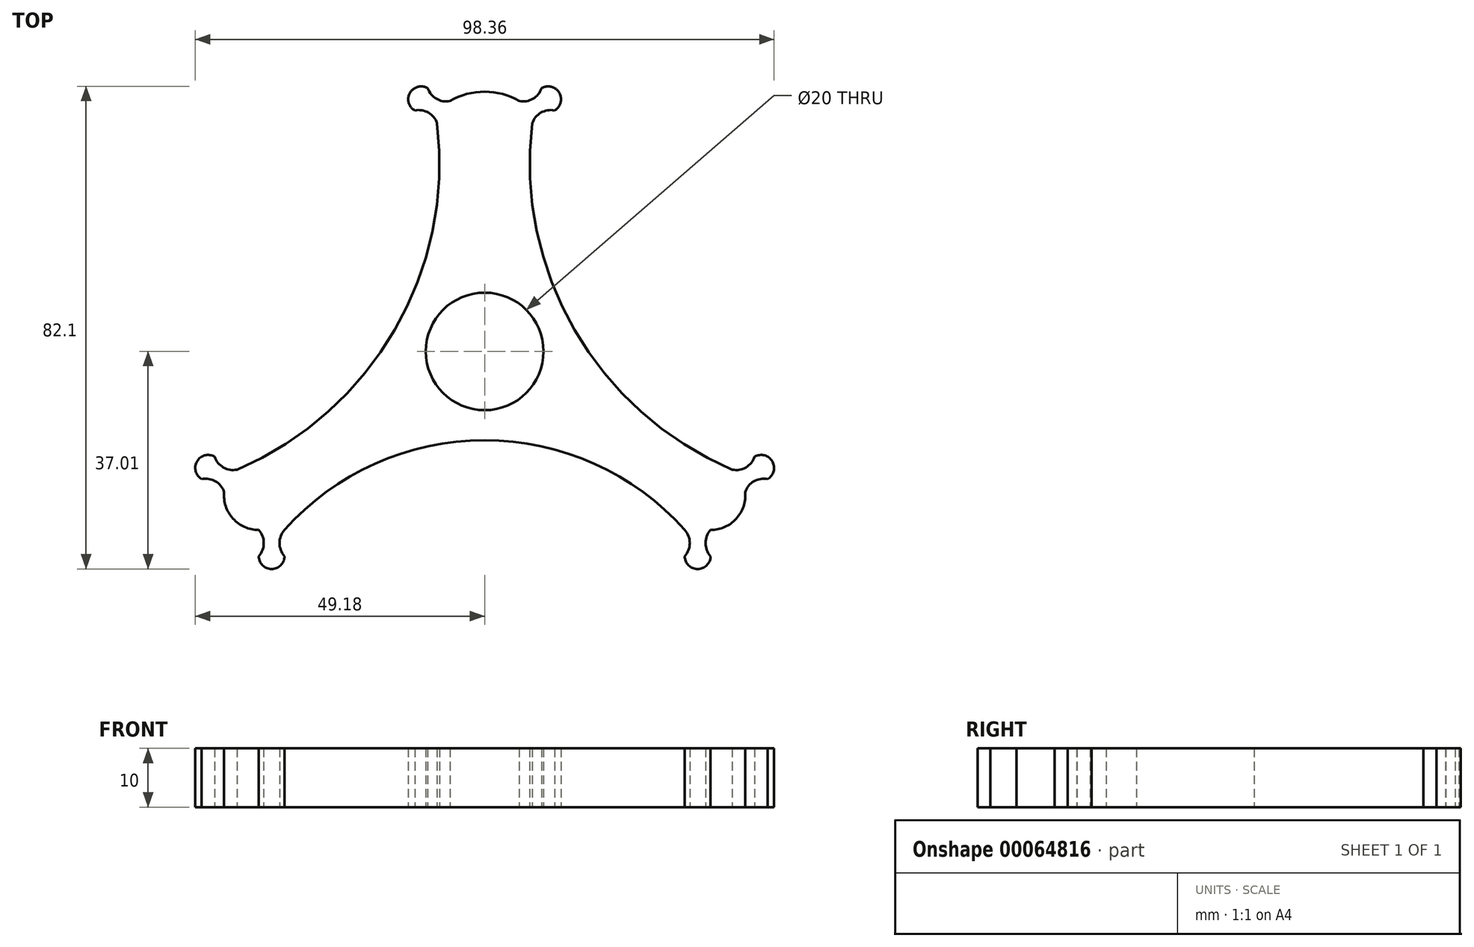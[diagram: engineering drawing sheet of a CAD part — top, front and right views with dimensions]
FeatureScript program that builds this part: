
annotation { "Feature Type Name" : "Feature", "Feature Type Description" : "" }
export const myFeature = defineFeature(function(context is Context, id is Id, definition is map)
    precondition{}
    {
        {
            var Q0;
            Q0=qCreatedBy(makeId("Top.planeOp"),FACE);
            var sketch = newSketch(context, id + "F0", { "sketchPlane" : qUnion([Q0])});
            skCircle(sketch, "E0", {"center": v(0, 0) * mm, "radius": 10 * mm});
            skCircle(sketch, "E1", {"center": v(0, 0) * mm, "radius": 15 * mm});
            skPoint(sketch, "E2", {"position": v(-25.07, 9.34) * mm});
            skLineSegment(sketch, "E3", {"start": v(-25.07, 9.34) * mm, "end": v(-8.07, 38.78) * mm, "construction": true});
            skLineSegment(sketch, "E4", {"start": v(-25.07, 9.34) * mm, "end": v(-42.07, -20.1) * mm, "construction": true});
            skLineSegment(sketch, "E5.MirrorCS", {"start": v(25.07, 9.34) * mm, "end": v(8.07, 38.78) * mm, "construction": true});
            skLineSegment(sketch, "E6.MirrorCS", {"start": v(25.07, 9.34) * mm, "end": v(42.07, -20.1) * mm, "construction": true});
            skLineSegment(sketch, "E7", {"start": v(0, -30.38) * mm, "end": v(-34, -30.38) * mm, "construction": true});
            skPoint(sketch, "E8", {"position": v(0, -30.38) * mm});
            skLineSegment(sketch, "E9", {"start": v(0, -30.38) * mm, "end": v(34, -30.38) * mm, "construction": true});
            skPoint(sketch, "E10", {"position": v(-5.87, 42.6) * mm});
            skPoint(sketch, "E11", {"position": v(-44.27, -23.92) * mm});
            skPoint(sketch, "E12.MirrorP", {"position": v(5.87, 42.6) * mm});
            skPoint(sketch, "E13.MirrorP", {"position": v(44.27, -23.92) * mm});
            skPoint(sketch, "E14", {"position": v(-38.4, -30.38) * mm});
            skPoint(sketch, "E15", {"position": v(38.4, -30.38) * mm});
            skLineSegment(sketch, "E16", {"start": v(-25.07, 9.34) * mm, "end": v(-30.13, 12.26) * mm});
            skLineSegment(sketch, "E17", {"start": v(25.07, 9.34) * mm, "end": v(27.99, 11.02) * mm});
            skLineSegment(sketch, "E18", {"start": v(0, -30.38) * mm, "end": v(0, -34.69) * mm});
            skArc(sketch, "E19", {"start": v(8.07, 38.78) * mm, "mid": v(15.27, 3.68) * mm, "end": v(42.07, -20.1) * mm});
            skArc(sketch, "E20.MirrorCS", {"start": v(-8.07, 38.78) * mm, "mid": v(-15.27, 3.68) * mm, "end": v(-42.07, -20.1) * mm});
            skArc(sketch, "E21", {"start": v(34, -30.38) * mm, "mid": v(0, -15.12) * mm, "end": v(-34, -30.38) * mm});
            skArc(sketch, "E22", {"start": v(-38.4, -34.83) * mm, "mid": v(-37.54, -32.6) * mm, "end": v(-38.4, -30.38) * mm});
            skArc(sketch, "E23.MirrorCS", {"start": v(-34, -34.83) * mm, "mid": v(-34.86, -32.6) * mm, "end": v(-34, -30.38) * mm});
            skArc(sketch, "E24", {"start": v(-38.4, -34.83) * mm, "mid": v(-36.2, -37.01) * mm, "end": v(-34, -34.83) * mm});
            skArc(sketch, "E25.MirrorCS", {"start": v(34, -34.83) * mm, "mid": v(34.86, -32.6) * mm, "end": v(34, -30.38) * mm});
            skArc(sketch, "E26.MirrorCS", {"start": v(38.4, -34.83) * mm, "mid": v(37.54, -32.6) * mm, "end": v(38.4, -30.38) * mm});
            skArc(sketch, "E27.MirrorCS", {"start": v(38.4, -34.83) * mm, "mid": v(36.2, -37.01) * mm, "end": v(34, -34.83) * mm});
            skArc(sketch, "E28", {"start": v(-44.27, -23.92) * mm, "mid": v(-45.76, -22.1) * mm, "end": v(-48.08, -21.72) * mm});
            skArc(sketch, "E29", {"start": v(-45.88, -17.9) * mm, "mid": v(-44.4, -19.73) * mm, "end": v(-42.07, -20.1) * mm});
            skArc(sketch, "E30", {"start": v(-45.88, -17.9) * mm, "mid": v(-48.89, -18.71) * mm, "end": v(-48.08, -21.72) * mm});
            skArc(sketch, "E31", {"start": v(-44.27, -23.92) * mm, "mid": v(-42.77, -28.45) * mm, "end": v(-38.4, -30.38) * mm});
            skArc(sketch, "E32.MirrorCS", {"start": v(-11.88, 40.98) * mm, "mid": v(-9.56, 40.6) * mm, "end": v(-8.07, 38.78) * mm});
            skArc(sketch, "E33.MirrorCS", {"start": v(-5.87, 42.6) * mm, "mid": v(-8.2, 42.97) * mm, "end": v(-9.68, 44.8) * mm});
            skArc(sketch, "E34.MirrorCS", {"start": v(-11.88, 40.98) * mm, "mid": v(-12.69, 43.99) * mm, "end": v(-9.68, 44.8) * mm});
            skArc(sketch, "E35.MirrorCS", {"start": v(5.87, 42.6) * mm, "mid": v(8.2, 42.97) * mm, "end": v(9.68, 44.8) * mm});
            skArc(sketch, "E36.MirrorCS", {"start": v(11.88, 40.98) * mm, "mid": v(9.56, 40.6) * mm, "end": v(8.07, 38.78) * mm});
            skArc(sketch, "E37.MirrorCS", {"start": v(11.88, 40.98) * mm, "mid": v(12.69, 43.99) * mm, "end": v(9.68, 44.8) * mm});
            skArc(sketch, "E38.MirrorCS", {"start": v(45.88, -17.9) * mm, "mid": v(44.4, -19.73) * mm, "end": v(42.07, -20.1) * mm});
            skArc(sketch, "E39.MirrorCS", {"start": v(44.27, -23.92) * mm, "mid": v(45.76, -22.1) * mm, "end": v(48.08, -21.72) * mm});
            skArc(sketch, "E40.MirrorCS", {"start": v(45.88, -17.9) * mm, "mid": v(48.89, -18.71) * mm, "end": v(48.08, -21.72) * mm});
            skArc(sketch, "E41.MirrorCS", {"start": v(44.27, -23.92) * mm, "mid": v(42.77, -28.45) * mm, "end": v(38.4, -30.38) * mm});
            skArc(sketch, "E42", {"start": v(5.87, 42.6) * mm, "mid": v(0, 44.18) * mm, "end": v(-5.87, 42.6) * mm});
            skSolve(sketch);
        }
        {
            var Q0;
            Q0=makeQuery(id+"F0.imprint","IMPRINT",FACE,{"disambiguationData":[TD([[makeQuery(id+"F0.imprint","IMPRINT",EDGE,{"derivedFrom":sQuery(id+"F0.wireOp",EDGE,"E0")}),-1.0]])]});
            var Q1;
            Q1=makeQuery(id+"F0.imprint","IMPRINT",FACE,{"disambiguationData":[TD([[makeQuery(id+"F0.imprint","IMPRINT",EDGE,{"derivedFrom":sQuery(id+"F0.wireOp",EDGE,"E1")}),-1.0]])]});
            var Q2;
            Q2=makeQuery(id+"F0.imprint","IMPRINT",FACE,{"disambiguationData":[TD([[makeQuery(id+"F0.imprint","IMPRINT",EDGE,{"derivedFrom":sQuery(id+"F0.wireOp",EDGE,"rauPZceA-AvJe-wY7d-aHQx-y0BkBm7dZX6A")}),1.0]])]});
            var Q3;
            {var subQ0=sQuery(id+"F0.wireOp",EDGE,"66c77fe6-8d23-4775-9337-49077d0eecb40.MirrorCS");Q3=makeQuery(id+"F0.imprint","IMPRINT",FACE,{"disambiguationData":[TD([[makeQuery(id+"F0.imprint","IMPRINT",EDGE,{"derivedFrom":subQ0}),-1.0]])]});}
            var Q4;
            {var subQ0=sQuery(id+"F0.wireOp",EDGE,"f178b5fa-dc7a-4bd1-90cf-9f9022b9a26d0.MirrorCS");Q4=makeQuery(id+"F0.imprint","IMPRINT",FACE,{"disambiguationData":[TD([[makeQuery(id+"F0.imprint","IMPRINT",EDGE,{"derivedFrom":subQ0}),1.0]])]});}
            var Q5;
            {var subQ0=sQuery(id+"F0.wireOp",EDGE,"766df824-92d9-44e2-9a4e-65756bf51aea");var subQ1=makeQuery(id+"F0.imprint","INTERSECT",VERTEX,{"derivedFrom":[subQ0,sQuery(id+"F0.wireOp",EDGE,"f178b5fa-dc7a-4bd1-90cf-9f9022b9a26d0.MirrorCS")]});Q5=makeQuery(id+"F0.imprint","IMPRINT",FACE,{"disambiguationData":[TD([[makeQuery(id+"F0.imprint","IMPRINT",EDGE,{"disambiguationData":[TD([[subQ1,-1.0]])],"derivedFrom":subQ0}),1.0]])]});}
            var Q6;
            {var subQ0=sQuery(id+"F0.wireOp",EDGE,"218adaf4-7306-4dce-b0c2-e02d0b1e01730.MirrorCS");Q6=makeQuery(id+"F0.imprint","IMPRINT",FACE,{"disambiguationData":[TD([[makeQuery(id+"F0.imprint","IMPRINT",EDGE,{"derivedFrom":subQ0}),-1.0]])]});}
            var Q7;
            {var subQ0=sQuery(id+"F0.wireOp",EDGE,"57e329e2-70f2-4a0c-8648-4a172ac2a8620.MirrorCS");Q7=makeQuery(id+"F0.imprint","IMPRINT",FACE,{"disambiguationData":[TD([[makeQuery(id+"F0.imprint","IMPRINT",EDGE,{"derivedFrom":subQ0}),1.0]])]});}
            var Q8;
            {var subQ0=sQuery(id+"F0.wireOp",EDGE,"7f4108d4-b1d3-4f68-b26e-f25bcda3abed");var subQ1=makeQuery(id+"F0.imprint","INTERSECT",VERTEX,{"derivedFrom":[subQ0,sQuery(id+"F0.wireOp",EDGE,"57e329e2-70f2-4a0c-8648-4a172ac2a8620.MirrorCS")]});Q8=makeQuery(id+"F0.imprint","IMPRINT",FACE,{"disambiguationData":[TD([[makeQuery(id+"F0.imprint","IMPRINT",EDGE,{"disambiguationData":[TD([[subQ1,-1.0]])],"derivedFrom":subQ0}),1.0]])]});}
            var Q9;
            {var subQ0=sQuery(id+"F0.wireOp",EDGE,"7BR6bjah-HHM2-aaMn-V7ne-WDie43C7rssP");Q9=makeQuery(id+"F0.imprint","IMPRINT",FACE,{"disambiguationData":[TD([[makeQuery(id+"F0.imprint","IMPRINT",EDGE,{"derivedFrom":subQ0}),-1.0]])]});}
            var Q10;
            {var subQ0=sQuery(id+"F0.wireOp",EDGE,"68eed4c9-a6f2-48c1-af04-7bd5d963a1a60.MirrorCS");Q10=makeQuery(id+"F0.imprint","IMPRINT",FACE,{"disambiguationData":[TD([[makeQuery(id+"F0.imprint","IMPRINT",EDGE,{"derivedFrom":subQ0}),1.0]])]});}
            var Q11;
            {var subQ4=sQuery(id+"F0.wireOp",EDGE,"ZnVcgLQC-YPiM-oc29-vfqV-L4HdhOj6Hgbx");Q11=makeQuery(id+"F0.imprint","IMPRINT",FACE,{"disambiguationData":[TD([[makeQuery(id+"F0.imprint","IMPRINT",EDGE,{"derivedFrom":subQ4}),1.0]])]});}
            var Q12;
            {var subQ0=sQuery(id+"F0.wireOp",EDGE,"ZnVcgLQC-YPiM-oc29-vfqV-L4HdhOj6Hgbx");Q12=makeQuery(id+"F0.imprint","IMPRINT",FACE,{"disambiguationData":[TD([[makeQuery(id+"F0.imprint","IMPRINT",EDGE,{"derivedFrom":subQ0}),-1.0]])]});}
            var Q13;
            {var subQ0=sQuery(id+"F0.wireOp",EDGE,"e4d09ac3-73be-4e2f-9fd0-e6afb1f81fb40.MirrorC");var subQ1=makeQuery(id+"F0.imprint","INTERSECT",VERTEX,{"derivedFrom":[subQ0,sQuery(id+"F0.wireOp",EDGE,"GvBOSrXI-6s7b-nos9-OxcZ-QlSHfa4bqhK4")]});Q13=makeQuery(id+"F0.imprint","IMPRINT",FACE,{"disambiguationData":[TD([[makeQuery(id+"F0.imprint","IMPRINT",EDGE,{"disambiguationData":[TD([[subQ1,-1.0]])],"derivedFrom":subQ0}),-1.0]])]});}
            var Q14;
            Q14=makeQuery(id+"F0.imprint","IMPRINT",FACE,{"disambiguationData":[TD([[makeQuery(id+"F0.imprint","IMPRINT",EDGE,{"derivedFrom":sQuery(id+"F0.wireOp",EDGE,"hSSR9ah8-QHQd-FjbW-g9Ed-Mq7VvAuAAHpD")}),-1.0]])]});
            var Q15;
            Q15=makeQuery(id+"F0.imprint","IMPRINT",FACE,{"disambiguationData":[TD([[makeQuery(id+"F0.imprint","IMPRINT",EDGE,{"derivedFrom":sQuery(id+"F0.wireOp",EDGE,"jAYGnJXh-nT1b-cXTS-xOFE-wMPNsA0xjkUn")}),-1.0]])]});
            var Q16;
            Q16=makeQuery(id+"F0.imprint","IMPRINT",FACE,{"disambiguationData":[TD([[makeQuery(id+"F0.imprint","IMPRINT",EDGE,{"derivedFrom":sQuery(id+"F0.wireOp",EDGE,"a5MMVbLW-wkiR-7yXn-SqoQ-ujKSQeReURW1")}),-1.0]])]});
            var Q17;
            {var subQ0=sQuery(id+"F0.wireOp",EDGE,"0805d99d-395f-4948-bb78-e127530f8ec20.MirrorC");var subQ1=makeQuery(id+"F0.imprint","INTERSECT",VERTEX,{"derivedFrom":[subQ0,sQuery(id+"F0.wireOp",EDGE,"a9e64960-8553-4fb6-9a36-3d952f51e22b0.MirrorCS")]});Q17=makeQuery(id+"F0.imprint","IMPRINT",FACE,{"disambiguationData":[TD([[makeQuery(id+"F0.imprint","IMPRINT",EDGE,{"disambiguationData":[TD([[subQ1,-1.0]])],"derivedFrom":subQ0}),-1.0]])]});}
            var Q18;
            {var subQ0=sQuery(id+"F0.wireOp",EDGE,"a9e64960-8553-4fb6-9a36-3d952f51e22b0.MirrorCS");Q18=makeQuery(id+"F0.imprint","IMPRINT",FACE,{"disambiguationData":[TD([[makeQuery(id+"F0.imprint","IMPRINT",EDGE,{"derivedFrom":subQ0}),-1.0]])]});}
            var Q19;
            {var subQ0=sQuery(id+"F0.wireOp",EDGE,"37fa7e79-00de-424d-aafe-a6521ed99ab80.MirrorCS");Q19=makeQuery(id+"F0.imprint","IMPRINT",FACE,{"disambiguationData":[TD([[makeQuery(id+"F0.imprint","IMPRINT",EDGE,{"derivedFrom":subQ0}),1.0]])]});}
            var Q20;
            {var subQ0=sQuery(id+"F0.wireOp",EDGE,"4bdbab69-e935-48e3-9672-c75c17e436940.MirrorCS");Q20=makeQuery(id+"F0.imprint","IMPRINT",FACE,{"disambiguationData":[TD([[makeQuery(id+"F0.imprint","IMPRINT",EDGE,{"derivedFrom":subQ0}),1.0]])]});}
            var Q21;
            {var subQ0=sQuery(id+"F0.wireOp",EDGE,"3c36e450-a305-4c08-9761-fcd4eeef911e0.MirrorCS");Q21=makeQuery(id+"F0.imprint","IMPRINT",FACE,{"disambiguationData":[TD([[makeQuery(id+"F0.imprint","IMPRINT",EDGE,{"derivedFrom":subQ0}),-1.0]])]});}
            var Q22;
            {var subQ0=sQuery(id+"F0.wireOp",EDGE,"8e0ed5d7-1bba-42ff-a766-a8121d5b3dc6");var subQ1=makeQuery(id+"F0.imprint","INTERSECT",VERTEX,{"derivedFrom":[subQ0,sQuery(id+"F0.wireOp",EDGE,"4bdbab69-e935-48e3-9672-c75c17e436940.MirrorCS")]});Q22=makeQuery(id+"F0.imprint","IMPRINT",FACE,{"disambiguationData":[TD([[makeQuery(id+"F0.imprint","IMPRINT",EDGE,{"disambiguationData":[TD([[subQ1,-1.0]])],"derivedFrom":subQ0}),1.0]])]});}
            extrude(context, id + "F1", {"entities" : qUnion([Q0, Q1, Q2, Q3, Q4, Q5, Q6, Q7, Q8, Q9, Q10, Q11, Q12, Q13, Q14, Q15, Q16, Q17, Q18, Q19, Q20, Q21, Q22]), "depth" : 10 * mm});
        }
    });
